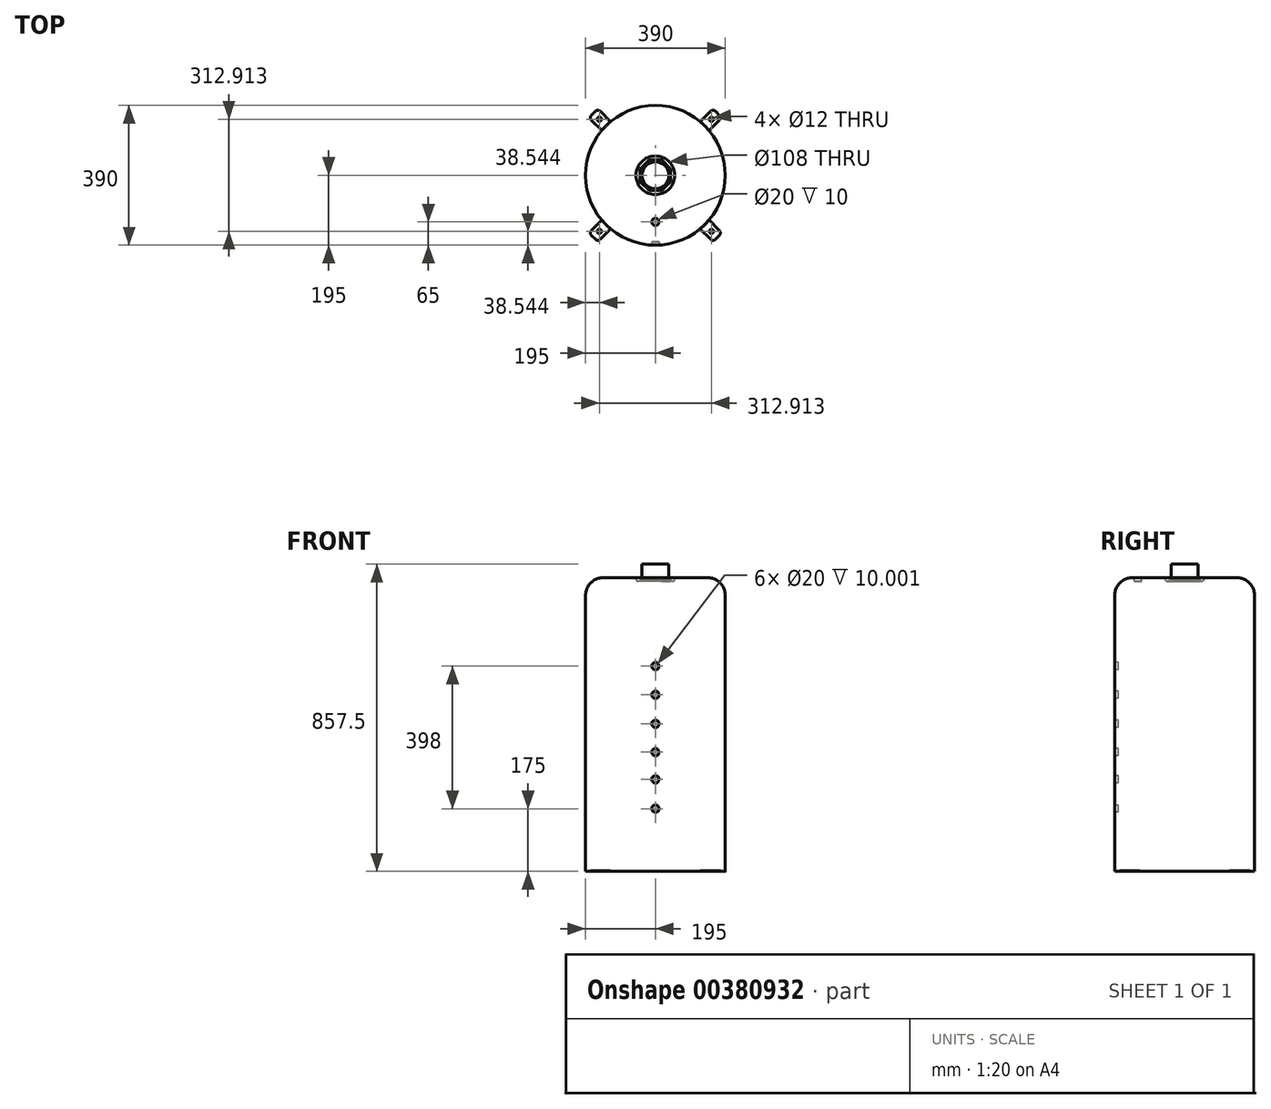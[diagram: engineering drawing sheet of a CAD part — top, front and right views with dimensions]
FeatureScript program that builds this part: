
annotation { "Feature Type Name" : "Feature", "Feature Type Description" : "" }
export const myFeature = defineFeature(function(context is Context, id is Id, definition is map)
    precondition{}
    {
        {
            var Q0;
            Q0=qCreatedBy(makeId("Top.planeOp"),FACE);
            cPlane(context, id + "F0", {"entities" : qUnion([Q0]), "cplaneType" : CPlaneType.OFFSET, "offset" : 820 * mm, "width" : 152.4 * mm, "height" : 152.4 * mm});
        }
        {
            var Q0;
            Q0=qCreatedBy(makeId("Front.planeOp"),FACE);
            var sketch = newSketch(context, id + "F1", { "sketchPlane" : qUnion([Q0])});
            skLineSegment(sketch, "E0", {"start": v(0, 0) * mm, "end": v(195, 0) * mm});
            skLineSegment(sketch, "E1", {"start": v(195, 0) * mm, "end": v(195, 770) * mm});
            skLineSegment(sketch, "E2", {"start": v(0, 820) * mm, "end": v(145, 820) * mm});
            skPoint(sketch, "E3.visualSharp", {"position": v(195, 820) * mm});
            skArc(sketch, "E3.filletArc", {"start": v(195, 770) * mm, "mid": v(180.36, 805.36) * mm, "end": v(145, 820) * mm});
            skLineSegment(sketch, "E4", {"start": v(0, 820) * mm, "end": v(0, 0) * mm});
            skSolve(sketch);
        }
        {
            var Q0;
            Q0=makeQuery(id+"F1.imprint","IMPRINT",FACE,{"disambiguationData":[TD([[makeQuery(id+"F1.imprint","IMPRINT",EDGE,{"derivedFrom":sQuery(id+"F1.wireOp",EDGE,"E0")}),1.0]])]});
            var Q1;
            Q1=sQuery(id+"F1.wireOp",EDGE,"E4");
            revolve(context, id + "F2", {"entities" : qUnion([Q0]), "axis" : qUnion([Q1]), "revolveType" : RevolveType.FULL});
        }
        {
            var Q0;
            Q0=makeQuery(id+"F2.opRevolve","SWEPT_FACE",FACE,{"disambiguationData":[OSD([sQuery(id+"F1.wireOp",EDGE,"E2")])]});
            var sketch = newSketch(context, id + "F3", { "sketchPlane" : qUnion([Q0])});
            skCircle(sketch, "E5", {"center": v(0, 0) * mm, "radius": 54 * mm});
            skSolve(sketch);
        }
        {
            var Q0;
            Q0=makeQuery(id+"F3.imprint","IMPRINT",FACE,{"disambiguationData":[TD([[makeQuery(id+"F3.imprint","IMPRINT",EDGE,{"derivedFrom":sQuery(id+"F3.wireOp",EDGE,"E5")}),1.0]])]});
            var Q1;
            Q1=sQuery(id+"F3.wireOp",EDGE,"E5");
            extrude(context, id + "F4", {"entities" : qUnion([Q0]), "operationType" : NewBodyOperationType.REMOVE, "surfaceEntities" : qUnion([Q1]), "oppositeDirection" : true, "depth" : 10 * mm});
        }
        {
            var Q0;
            Q0=makeQuery(id+"F4.boolean.opBoolean","COPY",EDGE,{"derivedFrom":makeQuery(id+"F4.opExtrude","CAP_EDGE",EDGE,{"disambiguationData":[OSD([sQuery(id+"F3.wireOp",EDGE,"E5")])],"isStart":true})});
            var Q1;
            Q1=makeQuery(id+"F4.boolean.opBoolean","COPY",EDGE,{"derivedFrom":makeQuery(id+"F4.opExtrude","CAP_EDGE",EDGE,{"disambiguationData":[OSD([sQuery(id+"F3.wireOp",EDGE,"E5")])],"isStart":false})});
            fillet(context, id + "F5", {"entities" : qUnion([Q0, Q1]), "radius" : 5 * mm, "tangentPropagation" : true, "allowEdgeOverflow" : false});
        }
        {
            var Q0;
            Q0=makeQuery(id+"F4.boolean.opBoolean","COPY",FACE,{"derivedFrom":makeQuery(id+"F4.opExtrude","CAP_FACE",FACE,{"disambiguationData":[OSD([sQuery(id+"F3.wireOp",EDGE,"E5")])],"isStart":false})});
            var sketch = newSketch(context, id + "F6", { "sketchPlane" : qUnion([Q0])});
            skCircle(sketch, "E6.cCircle", {"center": v(0, 0) * mm, "radius": 42.5 * mm, "construction": true});
            skLineSegment(sketch, "E6.0", {"start": v(17.6, -42.5) * mm, "end": v(-17.6, -42.5) * mm});
            skLineSegment(sketch, "E6.1", {"start": v(-17.6, -42.5) * mm, "end": v(-42.5, -17.6) * mm});
            skLineSegment(sketch, "E6.2", {"start": v(-42.5, -17.6) * mm, "end": v(-42.5, 17.6) * mm});
            skLineSegment(sketch, "E6.3", {"start": v(-42.5, 17.6) * mm, "end": v(-17.6, 42.5) * mm});
            skLineSegment(sketch, "E6.4", {"start": v(-17.6, 42.5) * mm, "end": v(17.6, 42.5) * mm});
            skLineSegment(sketch, "E6.5", {"start": v(17.6, 42.5) * mm, "end": v(42.5, 17.6) * mm});
            skLineSegment(sketch, "E6.6", {"start": v(42.5, 17.6) * mm, "end": v(42.5, -17.6) * mm});
            skLineSegment(sketch, "E6.7", {"start": v(42.5, -17.6) * mm, "end": v(17.6, -42.5) * mm});
            skPoint(sketch, "E6.0.midPoint", {"position": v(0, -42.5) * mm});
            skSolve(sketch);
        }
        {
            var Q0;
            Q0=makeQuery(id+"F6.imprint","IMPRINT",FACE,{"disambiguationData":[TD([[makeQuery(id+"F6.imprint","IMPRINT",EDGE,{"derivedFrom":sQuery(id+"F6.wireOp",EDGE,"E6.0")}),-1.0]])]});
            extrude(context, id + "F7", {"entities" : qUnion([Q0]), "operationType" : NewBodyOperationType.ADD, "depth" : 5 * mm});
        }
        {
            var Q0;
            Q0=makeQuery(id+"F2.opRevolve","SWEPT_FACE",FACE,{"disambiguationData":[OSD([sQuery(id+"F1.wireOp",EDGE,"E2")])]});
            var sketch = newSketch(context, id + "F8", { "sketchPlane" : qUnion([Q0])});
            skCircle(sketch, "E7", {"center": v(0, 0) * mm, "radius": 37.5 * mm});
            skSolve(sketch);
        }
        {
            var Q0;
            Q0=makeQuery(id+"F8.imprint","IMPRINT",FACE,{"disambiguationData":[TD([[makeQuery(id+"F8.imprint","IMPRINT",EDGE,{"derivedFrom":sQuery(id+"F8.wireOp",EDGE,"E7")}),1.0]])]});
            extrude(context, id + "F9", {"entities" : qUnion([Q0]), "operationType" : NewBodyOperationType.ADD, "endBound" : BoundingType.SYMMETRIC, "depth" : 75 * mm});
        }
        {
            var Q0;
            Q0=qCreatedBy(makeId("Front.planeOp"),FACE);
            cPlane(context, id + "F10", {"entities" : qUnion([Q0]), "cplaneType" : CPlaneType.OFFSET, "offset" : (390 / 2) * mm, "width" : 152.4 * mm, "height" : 152.4 * mm});
        }
        {
            var Q0;
            Q0=qCreatedBy(id+"F10.planeOp",FACE);
            var sketch = newSketch(context, id + "F11", { "sketchPlane" : qUnion([Q0])});
            skLineSegment(sketch, "E8", {"start": v(0, 0) * mm, "end": v(0, 1710.38) * mm, "construction": true});
            skCircle(sketch, "E9", {"center": v(0, 175) * mm, "radius": 10 * mm});
            skCircle(sketch, "E10", {"center": v(0, 257) * mm, "radius": 10 * mm});
            skCircle(sketch, "E11", {"center": v(0, 333) * mm, "radius": 10 * mm});
            skCircle(sketch, "E12", {"center": v(0, 412) * mm, "radius": 10 * mm});
            skCircle(sketch, "E13", {"center": v(0, 493) * mm, "radius": 10 * mm});
            skCircle(sketch, "E14", {"center": v(0, 573) * mm, "radius": 10 * mm});
            skSolve(sketch);
        }
        {
            var Q0;
            Q0 = qSketchRegion(id + "F11", true);
            extrude(context, id + "F12", {"entities" : qUnion([Q0]), "operationType" : NewBodyOperationType.REMOVE, "oppositeDirection" : true, "depth" : 10 * mm});
        }
        {
            var Q0;
            Q0=makeQuery(id+"F2.opRevolve","SWEPT_FACE",FACE,{"disambiguationData":[OSD([sQuery(id+"F1.wireOp",EDGE,"E2")])]});
            var sketch = newSketch(context, id + "F13", { "sketchPlane" : qUnion([Q0])});
            skCircle(sketch, "E15", {"center": v(0, -130) * mm, "radius": 10 * mm});
            skSolve(sketch);
        }
        {
            var Q0;
            Q0 = qSketchRegion(id + "F13", true);
            extrude(context, id + "F14", {"entities" : qUnion([Q0]), "operationType" : NewBodyOperationType.REMOVE, "oppositeDirection" : true, "depth" : 10 * mm});
        }
        {
            var Q0;
            Q0=makeQuery(id+"F2.opRevolve","SWEPT_FACE",FACE,{"disambiguationData":[OSD([sQuery(id+"F1.wireOp",EDGE,"E0")])]});
            var sketch = newSketch(context, id + "F15", { "sketchPlane" : qUnion([Q0])});
            skLineSegment(sketch, "E16.top", {"start": v(-167.94, 178.54) * mm, "end": v(-178.54, 167.94) * mm});
            skLineSegment(sketch, "E16.left", {"start": v(-121.41, 146.16) * mm, "end": v(-153.8, 178.54) * mm});
            skLineSegment(sketch, "E16.right", {"start": v(-146.16, 121.41) * mm, "end": v(-178.54, 153.8) * mm});
            skPoint(sketch, "E16.middle", {"position": v(0, 0) * mm});
            skCircle(sketch, "E17", {"center": v(-156.46, 156.46) * mm, "radius": 6 * mm});
            skPoint(sketch, "E18.centerSnap0", {"position": v(0, -245) * mm});
            skLineSegment(sketch, "E19", {"start": v(-146.16, 121.41) * mm, "end": v(-121.41, 146.16) * mm});
            skPoint(sketch, "E20.orphan", {"position": v(-17.5, -245) * mm});
            skPoint(sketch, "E18.center.orphan", {"position": v(0, -223.39) * mm});
            skPoint(sketch, "E16.bottom.start.orphan", {"position": v(17.5, -245) * mm});
            skPoint(sketch, "E21.visualSharp", {"position": v(-160.87, 185.62) * mm});
            skArc(sketch, "E21.filletArc", {"start": v(-153.8, 178.54) * mm, "mid": v(-160.87, 181.47) * mm, "end": v(-167.94, 178.54) * mm});
            skPoint(sketch, "E22.visualSharp", {"position": v(-185.62, 160.87) * mm});
            skArc(sketch, "E22.filletArc", {"start": v(-178.54, 167.94) * mm, "mid": v(-181.47, 160.87) * mm, "end": v(-178.54, 153.8) * mm});
            skLineSegment(sketch, "E23.1.0", {"start": v(-121.41, -146.16) * mm, "end": v(-146.16, -121.41) * mm});
            skCircle(sketch, "E23.1.1", {"center": v(-156.46, -156.46) * mm, "radius": 6 * mm});
            skLineSegment(sketch, "E23.1.2", {"start": v(-146.16, -121.41) * mm, "end": v(-178.54, -153.8) * mm});
            skPoint(sketch, "E23.1.3", {"position": v(-160.87, -185.62) * mm});
            skPoint(sketch, "E23.1.4", {"position": v(-185.62, -160.87) * mm});
            skLineSegment(sketch, "E23.1.5", {"start": v(-121.41, -146.16) * mm, "end": v(-153.8, -178.54) * mm});
            skArc(sketch, "E23.1.6", {"start": v(-178.54, -153.8) * mm, "mid": v(-181.47, -160.87) * mm, "end": v(-178.54, -167.94) * mm});
            skArc(sketch, "E23.1.7", {"start": v(-167.94, -178.54) * mm, "mid": v(-160.87, -181.47) * mm, "end": v(-153.8, -178.54) * mm});
            skLineSegment(sketch, "E23.1.8", {"start": v(-178.54, -167.94) * mm, "end": v(-167.94, -178.54) * mm});
            skLineSegment(sketch, "E23.2.0", {"start": v(146.16, -121.41) * mm, "end": v(121.41, -146.16) * mm});
            skCircle(sketch, "E23.2.1", {"center": v(156.46, -156.46) * mm, "radius": 6 * mm});
            skLineSegment(sketch, "E23.2.2", {"start": v(121.41, -146.16) * mm, "end": v(153.8, -178.54) * mm});
            skPoint(sketch, "E23.2.3", {"position": v(185.62, -160.87) * mm});
            skPoint(sketch, "E23.2.4", {"position": v(160.87, -185.62) * mm});
            skLineSegment(sketch, "E23.2.5", {"start": v(146.16, -121.41) * mm, "end": v(178.54, -153.8) * mm});
            skArc(sketch, "E23.2.6", {"start": v(153.8, -178.54) * mm, "mid": v(160.87, -181.47) * mm, "end": v(167.94, -178.54) * mm});
            skArc(sketch, "E23.2.7", {"start": v(178.54, -167.94) * mm, "mid": v(181.47, -160.87) * mm, "end": v(178.54, -153.8) * mm});
            skLineSegment(sketch, "E23.2.8", {"start": v(167.94, -178.54) * mm, "end": v(178.54, -167.94) * mm});
            skLineSegment(sketch, "E23.3.0", {"start": v(121.41, 146.16) * mm, "end": v(146.16, 121.41) * mm});
            skCircle(sketch, "E23.3.1", {"center": v(156.46, 156.46) * mm, "radius": 6 * mm});
            skLineSegment(sketch, "E23.3.2", {"start": v(146.16, 121.41) * mm, "end": v(178.54, 153.8) * mm});
            skPoint(sketch, "E23.3.3", {"position": v(160.87, 185.62) * mm});
            skPoint(sketch, "E23.3.4", {"position": v(185.62, 160.87) * mm});
            skLineSegment(sketch, "E23.3.5", {"start": v(121.41, 146.16) * mm, "end": v(153.8, 178.54) * mm});
            skArc(sketch, "E23.3.6", {"start": v(178.54, 153.8) * mm, "mid": v(181.47, 160.87) * mm, "end": v(178.54, 167.94) * mm});
            skArc(sketch, "E23.3.7", {"start": v(167.94, 178.54) * mm, "mid": v(160.87, 181.47) * mm, "end": v(153.8, 178.54) * mm});
            skLineSegment(sketch, "E23.3.8", {"start": v(178.54, 167.94) * mm, "end": v(167.94, 178.54) * mm});
            skSolve(sketch);
        }
        {
            var Q0;
            Q0 = qSketchRegion(id + "F15", true);
            extrude(context, id + "F16", {"entities" : qUnion([Q0]), "operationType" : NewBodyOperationType.ADD, "oppositeDirection" : true, "depth" : 2 * mm});
        }
    });
